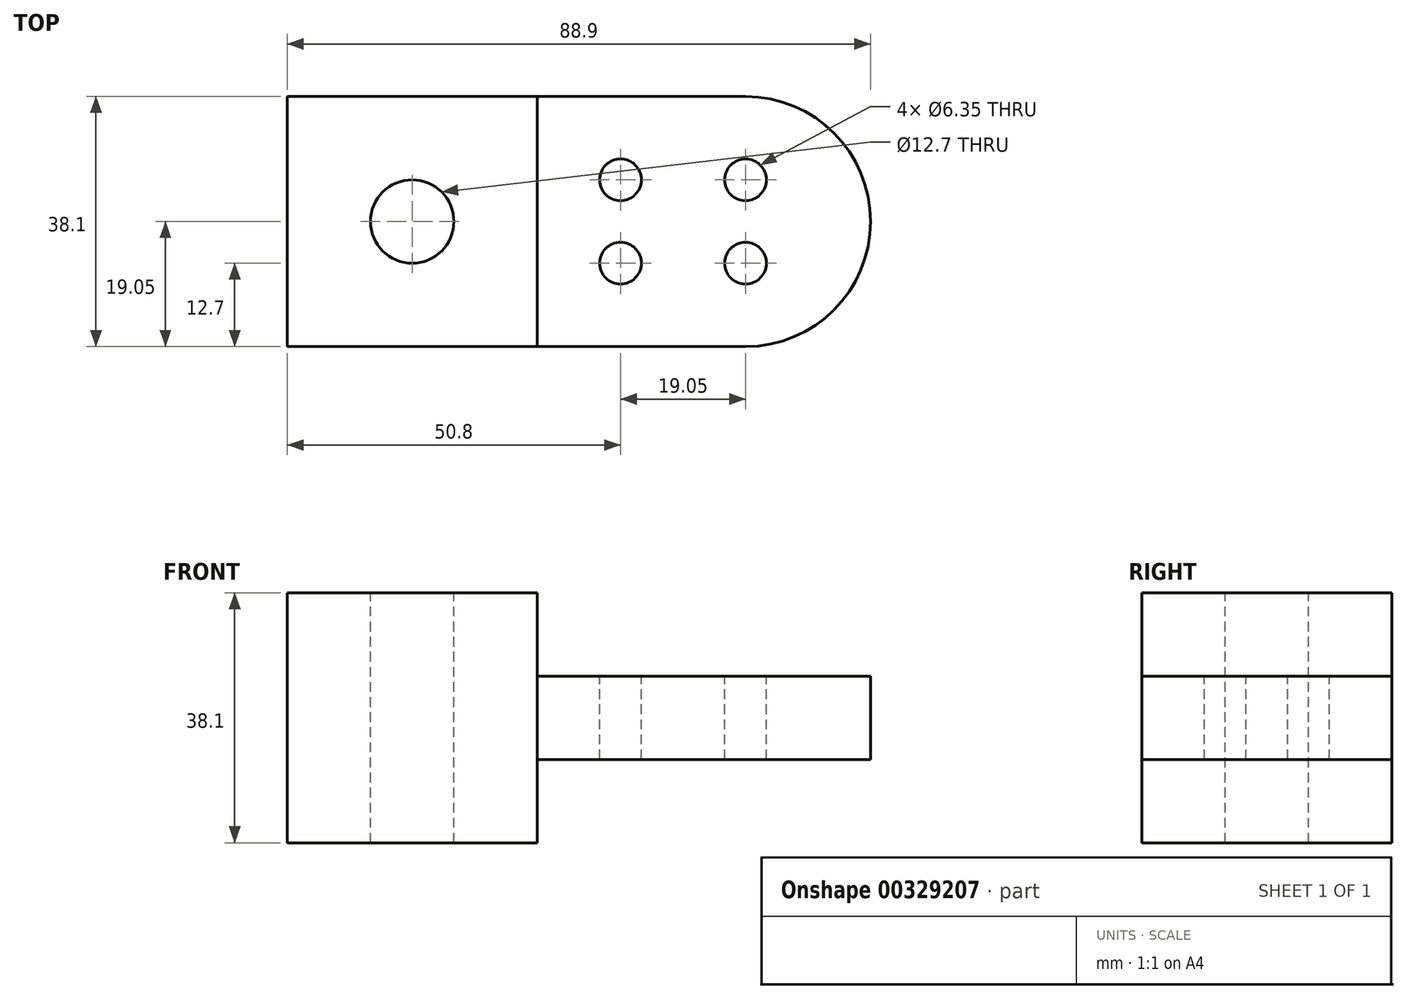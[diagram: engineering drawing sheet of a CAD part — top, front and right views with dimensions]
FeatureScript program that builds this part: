
annotation { "Feature Type Name" : "Feature", "Feature Type Description" : "" }
export const myFeature = defineFeature(function(context is Context, id is Id, definition is map)
    precondition{}
    {
        {
            var Q0;
            Q0=qCreatedBy(makeId("Top.planeOp"),FACE);
            var sketch = newSketch(context, id + "F0", { "sketchPlane" : qUnion([Q0])});
            skLineSegment(sketch, "E0", {"start": v(0, 0) * mm, "end": v(0, 38.1) * mm});
            skLineSegment(sketch, "E1", {"start": v(0, 38.1) * mm, "end": v(38.1, 38.1) * mm});
            skLineSegment(sketch, "E2", {"start": v(38.1, 38.1) * mm, "end": v(38.1, 0) * mm});
            skLineSegment(sketch, "E3", {"start": v(38.1, 0) * mm, "end": v(0, 0) * mm});
            skLineSegment(sketch, "E4", {"start": v(38.1, 38.1) * mm, "end": v(69.85, 38.1) * mm});
            skLineSegment(sketch, "E5", {"start": v(38.1, 0) * mm, "end": v(69.85, 0) * mm});
            skArc(sketch, "E6", {"start": v(69.85, 0) * mm, "mid": v(88.9, 19.05) * mm, "end": v(69.85, 38.1) * mm});
            skSolve(sketch);
        }
        {
            var Q0;
            Q0=makeQuery(id+"F0.imprint","IMPRINT",FACE,{"disambiguationData":[TD([[makeQuery(id+"F0.imprint","IMPRINT",EDGE,{"derivedFrom":sQuery(id+"F0.wireOp",EDGE,"E0")}),-1.0]])]});
            extrude(context, id + "F1", {"entities" : qUnion([Q0]), "depth" : 38.1 * mm});
        }
        {
            var Q0;
            Q0=makeQuery(id+"F0.imprint","IMPRINT",FACE,{"disambiguationData":[TD([[makeQuery(id+"F0.imprint","IMPRINT",EDGE,{"derivedFrom":sQuery(id+"F0.wireOp",EDGE,"E2")}),1.0]])]});
            extrude(context, id + "F2", {"entities" : qUnion([Q0]), "depth" : 25.4 * mm});
        }
        {
            var Q0;
            Q0=qCreatedBy(makeId("Front.planeOp"),FACE);
            var sketch = newSketch(context, id + "F3", { "sketchPlane" : qUnion([Q0])});
            skLineSegment(sketch, "E7", {"start": v(38.1, 12.7) * mm, "end": v(98.4, 12.7) * mm});
            skLineSegment(sketch, "E8", {"start": v(98.4, 12.7) * mm, "end": v(98.4, 0) * mm});
            skLineSegment(sketch, "E9", {"start": v(98.4, 0) * mm, "end": v(38.1, 0) * mm});
            skLineSegment(sketch, "E10", {"start": v(38.1, 0) * mm, "end": v(38.1, 12.7) * mm});
            skSolve(sketch);
        }
        {
            var Q0;
            Q0 = qSketchRegion(id + "F3", true);
            extrude(context, id + "F4", {"entities" : qUnion([Q0]), "operationType" : NewBodyOperationType.REMOVE, "endBound" : BoundingType.THROUGH_ALL, "oppositeDirection" : true, "depth" : 25.4 * mm});
        }
        {
            var Q0;
            Q0=makeQuery(id+"F1.opExtrude","CAP_FACE",FACE,{"disambiguationData":[OSD([sQuery(id+"F0.wireOp",EDGE,"E0"),sQuery(id+"F0.wireOp",EDGE,"E1"),sQuery(id+"F0.wireOp",EDGE,"E2"),sQuery(id+"F0.wireOp",EDGE,"E3")])],"isStart":false});
            var sketch = newSketch(context, id + "F5", { "sketchPlane" : qUnion([Q0])});
            skCircle(sketch, "E11", {"center": v(19.05, 19.05) * mm, "radius": 6.35 * mm});
            skSolve(sketch);
        }
        {
            var Q0;
            Q0 = qSketchRegion(id + "F5", true);
            extrude(context, id + "F6", {"entities" : qUnion([Q0]), "operationType" : NewBodyOperationType.REMOVE, "endBound" : BoundingType.THROUGH_ALL, "oppositeDirection" : true, "depth" : 25.4 * mm});
        }
        {
            var Q0;
            Q0=makeQuery(id+"F2.opExtrude","CAP_FACE",FACE,{"disambiguationData":[OSD([sQuery(id+"F0.wireOp",EDGE,"E2"),sQuery(id+"F0.wireOp",EDGE,"E4"),sQuery(id+"F0.wireOp",EDGE,"E5"),sQuery(id+"F0.wireOp",EDGE,"E6")])],"isStart":false});
            var sketch = newSketch(context, id + "F7", { "sketchPlane" : qUnion([Q0])});
            skCircle(sketch, "E12", {"center": v(50.8, 25.4) * mm, "radius": 3.18 * mm});
            skCircle(sketch, "E13", {"center": v(69.85, 25.4) * mm, "radius": 3.18 * mm});
            skCircle(sketch, "E14", {"center": v(50.8, 12.7) * mm, "radius": 3.18 * mm});
            skCircle(sketch, "E15", {"center": v(69.85, 12.7) * mm, "radius": 3.18 * mm});
            skSolve(sketch);
        }
        {
            var Q0;
            Q0 = qSketchRegion(id + "F7", true);
            extrude(context, id + "F8", {"entities" : qUnion([Q0]), "operationType" : NewBodyOperationType.REMOVE, "endBound" : BoundingType.THROUGH_ALL, "oppositeDirection" : true, "depth" : 25.4 * mm});
        }
    });
